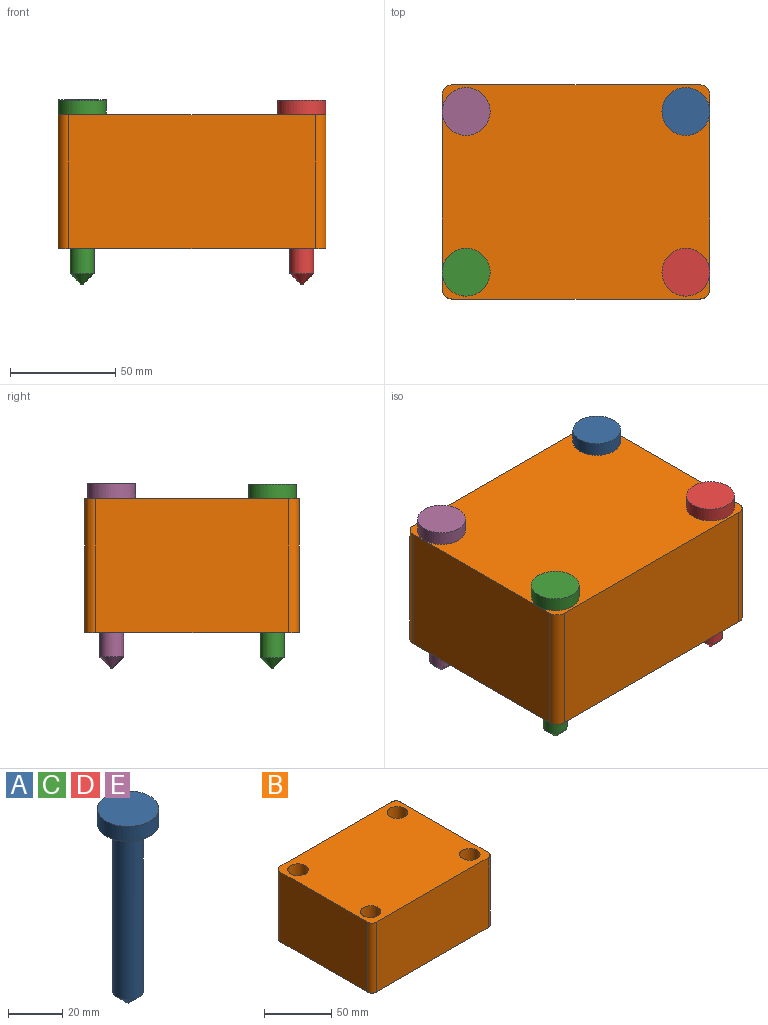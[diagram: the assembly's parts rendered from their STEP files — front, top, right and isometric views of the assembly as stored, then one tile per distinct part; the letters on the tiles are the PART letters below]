
ASSEMBLY  parts=5 mates=3
PART A: 6 faces, bbox 22.7x22.7x87.2 mm
  f0: plane 22.65x22.65mm, normal (0,0,1), area 402.9mm2, adj f1
  f1: cylinder r=11.33mm len=22.65mm, axis (0,0,-1), area 481.5mm2, adj f0,f2
  f2: plane 22.65x22.65mm, normal (0,0,-1), area 302.2mm2, adj f1,f3
  f3: cylinder r=5.66mm len=75.31mm, axis (0,0,-1), area 2679.5mm2, adj f2,f5
  f4: plane 1.17x1.17mm, normal (0,0,-1), area 1.1mm2, adj f5
  f5: cone r=0.58mm half-angle=45deg, axis (0,0,1), area 141mm2, adj f3,f4
PART B: 14 faces, bbox 127x101.6x63.5 mm
  f0: plane 116.84x63.5mm, normal (0,-1,0), area 7419.3mm2, adj f8,f9,f10,f13
  f1: plane 91.44x63.5mm, normal (1,0,0), area 5806.4mm2, adj f8,f9,f10,f11
  f2: plane 116.84x63.5mm, normal (0,1,0), area 7419.3mm2, adj f8,f9,f11,f12
  f3: cylinder r=7.62mm len=63.5mm, axis (0,0,-1), area 3040.2mm2, adj f8,f9
  f4: cylinder r=7.62mm len=63.5mm, axis (0,0,-1), area 3040.2mm2, adj f8,f9
  f5: cylinder r=7.62mm len=63.5mm, axis (0,0,-1), area 3040.2mm2, adj f8,f9
  f6: cylinder r=7.62mm len=63.5mm, axis (0,0,-1), area 3040.2mm2, adj f8,f9
  f7: plane 91.44x63.5mm, normal (-1,0,0), area 5806.4mm2, adj f8,f9,f12,f13
  f8: plane 127x101.6mm, normal (0,0,1), area 12151.4mm2, adj f0,f1,f2,f3,f4,f5,f6,f7
  f9: plane 127x101.6mm, normal (0,0,-1), area 12151.4mm2, adj f0,f1,f2,f3,f4,f5,f6,f7
  f10: cylinder r=5.08mm len=63.5mm, axis (0,0,1), area 506.7mm2, adj f0,f1,f8,f9
  f11: cylinder r=5.08mm len=63.5mm, axis (0,0,-1), area 506.7mm2, adj f1,f2,f8,f9
  f12: cylinder r=5.08mm len=63.5mm, axis (0,0,1), area 506.7mm2, adj f2,f7,f8,f9
  f13: cylinder r=5.08mm len=63.5mm, axis (0,0,-1), area 506.7mm2, adj f0,f7,f8,f9
PART C: same geometry as A
PART D: same geometry as A
PART E: same geometry as A
PLACE A at identity
PLACE B at identity fixed
PLACE C t=(-104.14,-76.2,0)mm
PLACE D t=(0,-76.2,0)mm
PLACE E rot(axis=(0,0,-1),0.5deg) t=(-104.46,0.45,0.3)mm
MATE fastened D.f1 <-> B.f5  axis (0,0,-1) through (52.07,-38.1,63.5)mm
MATE fastened C.f1 <-> B.f4  axis (0,0,-1) through (-52.07,-38.1,63.5)mm
MATE cylindrical E.f1 <-> B.f3  axis (0,0,-1) through (-52.07,38.1,63.8)mm
